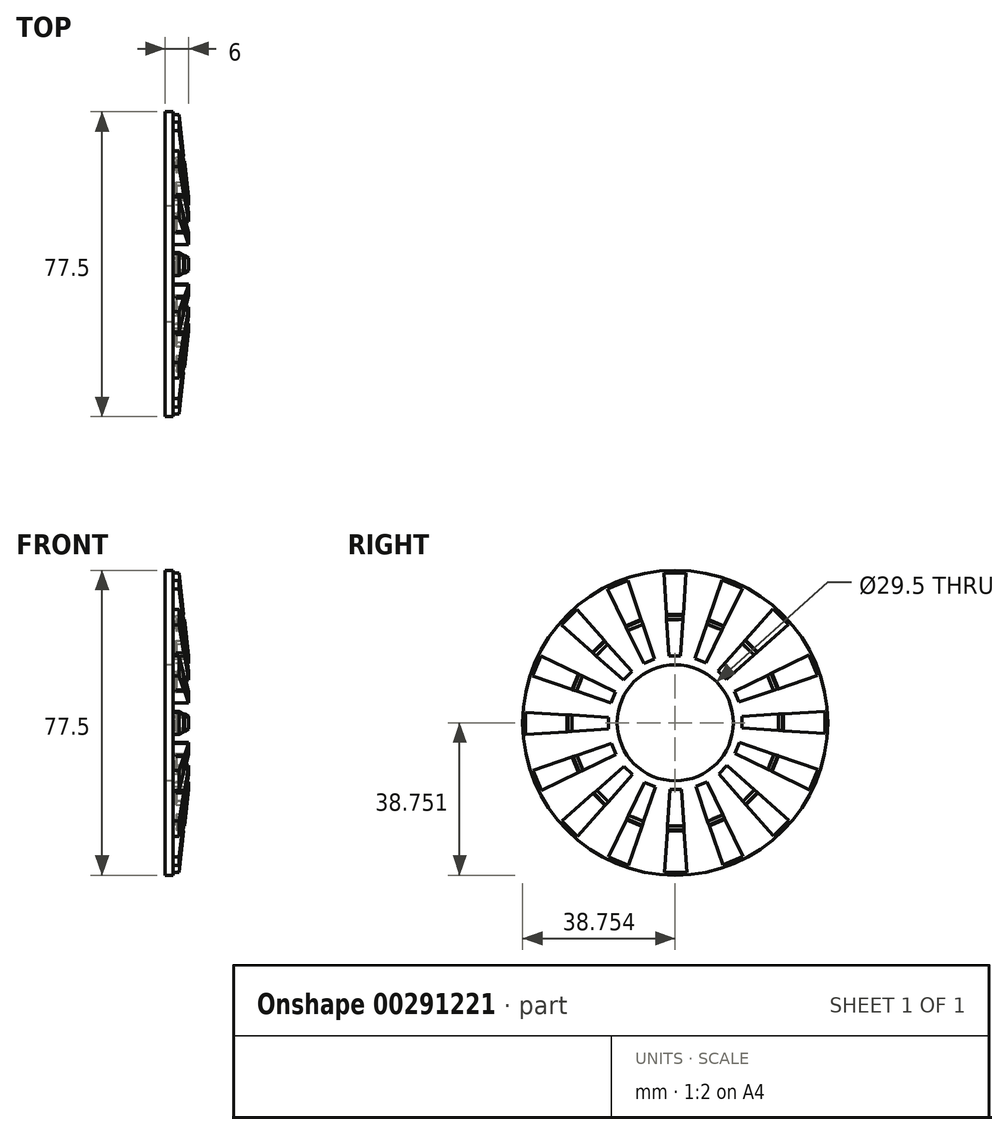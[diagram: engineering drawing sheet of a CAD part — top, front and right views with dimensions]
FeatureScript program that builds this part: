
annotation { "Feature Type Name" : "Feature", "Feature Type Description" : "" }
export const myFeature = defineFeature(function(context is Context, id is Id, definition is map)
    precondition{}
    {
        {
            var Q0;
            Q0=qCreatedBy(makeId("Front.planeOp"),FACE);
            var sketch = newSketch(context, id + "F0", { "sketchPlane" : qUnion([Q0])});
            skLineSegment(sketch, "E0", {"start": v(0, 0) * mm, "end": v(0, 21) * mm});
            skLineSegment(sketch, "E1", {"start": v(0, 21) * mm, "end": v(3.5, 21) * mm});
            skLineSegment(sketch, "E2", {"start": v(3.5, 21) * mm, "end": v(6, 0) * mm});
            skLineSegment(sketch, "E3", {"start": v(6, 0) * mm, "end": v(0, 0) * mm});
            skSolve(sketch);
        }
        {
            var Q0;
            Q0=qSketchRegion(id+"F0",true);
            extrude(context, id + "F1", {"entities" : qUnion([Q0]), "depth" : 6 * mm});
        }
        {
            var Q0;
            Q0=makeQuery(id+"F1.opExtrude","SWEPT_FACE",FACE,{"disambiguationData":[OSD([sQuery(id+"F0.wireOp",EDGE,"E2")])]});
            var sketch = newSketch(context, id + "F2", { "sketchPlane" : qUnion([Q0])});
            skLineSegment(sketch, "E4.bottom", {"start": v(-6, 9.86) * mm, "end": v(0, 9.86) * mm});
            skLineSegment(sketch, "E4.top", {"start": v(-6, 8.61) * mm, "end": v(0, 8.61) * mm});
            skLineSegment(sketch, "E4.left", {"start": v(-6, 9.86) * mm, "end": v(-6, 8.61) * mm});
            skLineSegment(sketch, "E4.right", {"start": v(0, 9.86) * mm, "end": v(0, 8.61) * mm});
            skSolve(sketch);
        }
        {
            var Q0;
            Q0=makeQuery(id+"F2.imprint","IMPRINT",FACE,{"disambiguationData":[TD([[makeQuery(id+"F2.imprint","IMPRINT",EDGE,{"derivedFrom":sQuery(id+"F2.wireOp",EDGE,"E4.bottom")}),-1.0]])]});
            extrude(context, id + "F3", {"entities" : qUnion([Q0]), "operationType" : NewBodyOperationType.REMOVE, "oppositeDirection" : true, "depth" : 2 * mm});
        }
        {
            var Q0;
            Q0=makeQuery(id+"F1.opExtrude","CAP_EDGE",EDGE,{"disambiguationData":[OSD([sQuery(id+"F0.wireOp",EDGE,"E3")])],"isStart":false});
            var Q1;
            Q1=makeQuery(id+"F1.opExtrude","CAP_EDGE",EDGE,{"disambiguationData":[OSD([sQuery(id+"F0.wireOp",EDGE,"E3")])],"isStart":true});
            chamfer(context, id + "F4", {"entities" : qUnion([Q0, Q1]), "chamferType" : ChamferType.TWO_OFFSETS, "width1" : 1.5 * mm, "oppositeDirection" : false, "width2" : 24.25 * mm, "tangentPropagation" : true});
        }
        {
            var Q0;
            Q0=qCreatedBy(makeId("Right.planeOp"),FACE);
            var sketch = newSketch(context, id + "F5", { "sketchPlane" : qUnion([Q0])});
            skLineSegment(sketch, "E5", {"start": v(-3, 0) * mm, "end": v(-2.88, -17) * mm});
            skCircle(sketch, "E6", {"center": v(-2.88, -17) * mm, "radius": 14.75 * mm});
            skCircle(sketch, "E7", {"center": v(-2.88, -17) * mm, "radius": 38.75 * mm});
            skSolve(sketch);
        }
        {
            var Q0;
            Q0=makeQuery(id+"F1.opExtrude","SWEPT_BODY",BODY,{"disambiguationData":[OSD([sQuery(id+"F0.wireOp",EDGE,"E0"),sQuery(id+"F0.wireOp",EDGE,"E1"),sQuery(id+"F0.wireOp",EDGE,"E2"),sQuery(id+"F0.wireOp",EDGE,"E3")])]});
            var Q1;
            Q1=sQuery(id+"F5.wireOp",EDGE,"E7");
            circularPattern(context, id + "F6", {"entities" : qUnion([Q0]), "axis" : qUnion([Q1]), "angle" : 360 * degree, "instanceCount" : 16, "equalSpace" : true});
        }
        {
            var Q0;
            Q0 = qSketchRegion(id + "F5", true);
            extrude(context, id + "F7", {"entities" : qUnion([Q0]), "operationType" : NewBodyOperationType.ADD, "depth" : 2 * mm});
        }
    });
